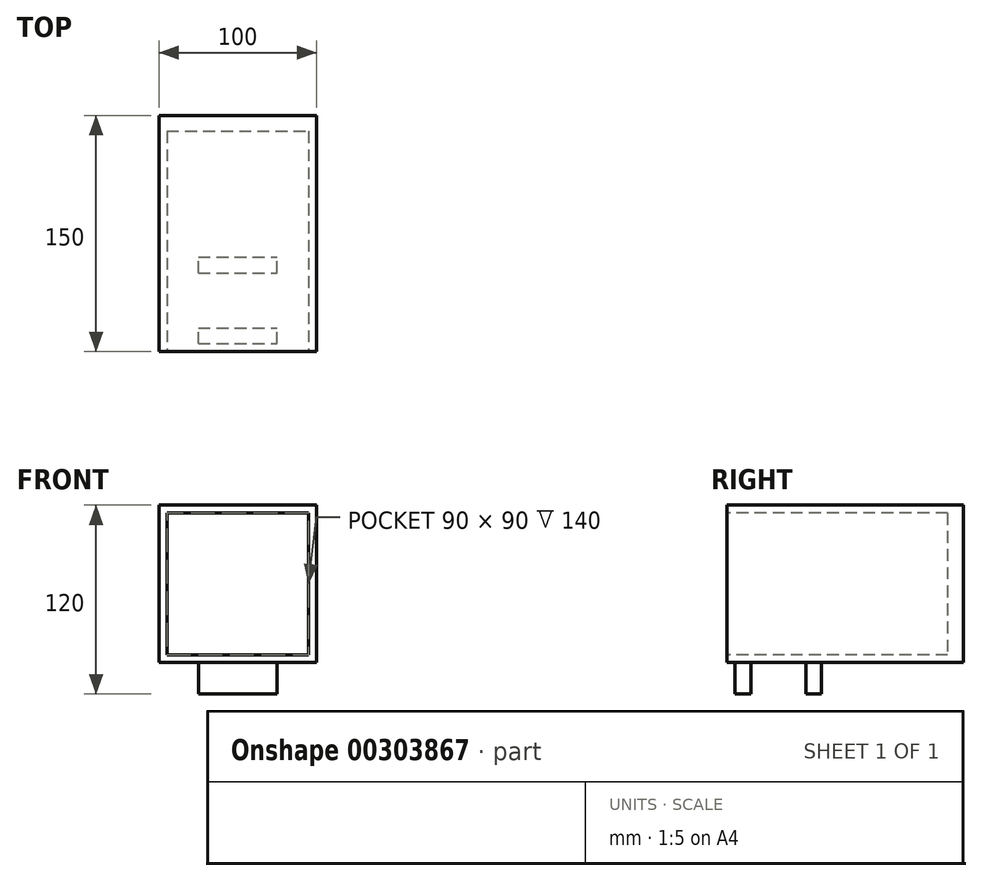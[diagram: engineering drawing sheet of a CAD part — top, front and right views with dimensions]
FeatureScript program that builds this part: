
annotation { "Feature Type Name" : "Feature", "Feature Type Description" : "" }
export const myFeature = defineFeature(function(context is Context, id is Id, definition is map)
    precondition{}
    {
        {
            var Q0;
            Q0=qCreatedBy(makeId("Front.planeOp"),FACE);
            var sketch = newSketch(context, id + "F0", { "sketchPlane" : qUnion([Q0])});
            skLineSegment(sketch, "E0.bottom", {"start": v(-49.37, 55.72) * mm, "end": v(50.63, 55.72) * mm});
            skLineSegment(sketch, "E0.top", {"start": v(-49.37, -44.28) * mm, "end": v(50.63, -44.28) * mm});
            skLineSegment(sketch, "E0.left", {"start": v(-49.37, 55.72) * mm, "end": v(-49.37, -44.28) * mm});
            skLineSegment(sketch, "E0.right", {"start": v(50.63, 55.72) * mm, "end": v(50.63, -44.28) * mm});
            skSolve(sketch);
        }
        {
            var Q0;
            Q0 = qSketchRegion(id + "F0", true);
            extrude(context, id + "F1", {"entities" : qUnion([Q0]), "depth" : 150 * mm});
        }
        {
            var Q0;
            Q0=makeQuery(id+"F1.opExtrude","CAP_FACE",FACE,{"disambiguationData":[OSD([sQuery(id+"F0.wireOp",EDGE,"E0.bottom"),sQuery(id+"F0.wireOp",EDGE,"E0.top"),sQuery(id+"F0.wireOp",EDGE,"E0.left"),sQuery(id+"F0.wireOp",EDGE,"E0.right")])],"isStart":false});
            var sketch = newSketch(context, id + "F2", { "sketchPlane" : qUnion([Q0])});
            skLineSegment(sketch, "E1.bottom", {"start": v(-44.37, 50.72) * mm, "end": v(45.63, 50.72) * mm});
            skLineSegment(sketch, "E1.top", {"start": v(-44.37, -39.28) * mm, "end": v(45.63, -39.28) * mm});
            skLineSegment(sketch, "E1.left", {"start": v(-44.37, 50.72) * mm, "end": v(-44.37, -39.28) * mm});
            skLineSegment(sketch, "E1.right", {"start": v(45.63, 50.72) * mm, "end": v(45.63, -39.28) * mm});
            skSolve(sketch);
        }
        {
            var Q0;
            Q0=makeQuery(id+"F2.imprint","IMPRINT",FACE,{"disambiguationData":[TD([[makeQuery(id+"F2.imprint","IMPRINT",EDGE,{"derivedFrom":sQuery(id+"F2.wireOp",EDGE,"E1.bottom")}),-1.0]])]});
            extrude(context, id + "F3", {"entities" : qUnion([Q0]), "operationType" : NewBodyOperationType.REMOVE, "oppositeDirection" : true, "depth" : 140 * mm});
        }
        {
            var Q0;
            Q0=makeQuery(id+"F1.opExtrude","SWEPT_FACE",FACE,{"disambiguationData":[OSD([sQuery(id+"F0.wireOp",EDGE,"E0.top")])]});
            var sketch = newSketch(context, id + "F4", { "sketchPlane" : qUnion([Q0])});
            skLineSegment(sketch, "E2.bottom", {"start": v(-24.37, 145) * mm, "end": v(25.63, 145) * mm});
            skLineSegment(sketch, "E2.top", {"start": v(-24.37, 90) * mm, "end": v(25.63, 90) * mm});
            skLineSegment(sketch, "E2.left", {"start": v(-24.37, 145) * mm, "end": v(-24.37, 90) * mm});
            skLineSegment(sketch, "E2.right", {"start": v(25.63, 145) * mm, "end": v(25.63, 90) * mm});
            skLineSegment(sketch, "E3.bottom", {"start": v(-24.37, 135) * mm, "end": v(25.63, 135) * mm});
            skLineSegment(sketch, "E3.top", {"start": v(-24.37, 100) * mm, "end": v(25.63, 100) * mm});
            skLineSegment(sketch, "E3.left", {"start": v(-24.37, 135) * mm, "end": v(-24.37, 100) * mm});
            skLineSegment(sketch, "E3.right", {"start": v(25.63, 135) * mm, "end": v(25.63, 100) * mm});
            skSolve(sketch);
        }
        {
            var Q0;
            {var subQ0=sQuery(id+"F4.wireOp",EDGE,"E2.bottom");Q0=makeQuery(id+"F4.imprint","IMPRINT",FACE,{"disambiguationData":[TD([[makeQuery(id+"F4.imprint","IMPRINT",EDGE,{"derivedFrom":subQ0}),-1.0]])]});}
            var Q1;
            {var subQ0=sQuery(id+"F4.wireOp",EDGE,"E2.top");Q1=makeQuery(id+"F4.imprint","IMPRINT",FACE,{"disambiguationData":[TD([[makeQuery(id+"F4.imprint","IMPRINT",EDGE,{"derivedFrom":subQ0}),1.0]])]});}
            extrude(context, id + "F5", {"entities" : qUnion([Q0, Q1]), "operationType" : NewBodyOperationType.ADD, "depth" : 20 * mm});
        }
    });
